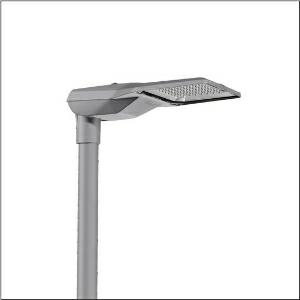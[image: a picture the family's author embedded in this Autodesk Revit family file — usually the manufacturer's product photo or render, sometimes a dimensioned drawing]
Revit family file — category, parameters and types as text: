
# Revit family: streetlight_sl_21_midi___st0_5a_5xe3b33s08lb_3b8c
name_source: partatom
category: Lighting Fixtures
units: mm (PartAtom-declared; Revit-internal decimal feet)

## family parameters
Cut with Voids When Loaded = No
Host = Face
Light Source = No
Part Type = Normal
Room Calculation Point = No
Round Connector Dimension = Use Diameter
Shared = No

## types (1)
- --- (1 x LED, 14340 lm, 99.6 W, 3000K)
    Apparent Load = 100 VA
    CIE Flux Codes = 41 75 97 100 100
    Color Rendering = 70
    Color Temperature = 3000K
    Default Elevation = 1800 mm
    Description = Streetlight SL 21 midi, mast luminaire, primary light control with lens, of PMMA, primary optical cover: cover, of toughened safety glass, transparent, light distribution: ST0.5a, light emission: direct distribution, primary light characteristic: asymmetric, installation type: side-entry, post-top, LED, High Power LED, rated luminous flux: 14.340lm, luminous efficacy: 144lm/W, light colour: 730, colour temperature: 3000K, control gear: D4i, control: overheat protection, constant luminous flux control, time-dependent luminous flux control, flexible luminous flux parameterisation, pre-setting: logarithmic dimming characteristic, mains connection: 230..240V, AC, 50/60Hz, start of lifetime: 100W, end of service life: 102W, reduction: 46W, luminaire housing, of diecast aluminium, powder-coated, Siteco® metallic grey (DB 702S), corrosivity category C5 mid according to DIN EN ISO 12944, please order mast flange separately, inclination adjustable: 0°, 5°, 10°, 15°, sealing non-destructively replaceable, multi-level sealing system, length: 644mm, width: 335mm, height: 110mm, mast flange for spigot size: 42mm (side-entry): 5XC10008XM4, 60/48mm (side-entry/post-top): 5XC10108XM2, 76/60mm (side-entry/post-top): 5XC10108XM1, mounting height: 4..8m, Smart Interface above, protection rating (complete): IP66, insulation class (complete): insulation class II (safety insulation), certification: CE, ENEC, ENEC+, VDE, impact resistance: IK10, permissible operating ambient temperature for outdoor applications: -40..+50°C, standard-compliant lighting for roads and squares, packaging unit: 1 piece

Light Distribution: ST0.5a
    Height = 111 mm
    Lamp = 1 x LED
    Lamp Light Flux = 14340 lm
    Lamp Power = 99.6 W
    Lamp count = 1
    Length = 644 mm
    Luminous efficacy = 144 lm/W
    Manufacturer = Siteco
    ModVariant = No
    Model = 5XE3B33S08LB
    Number of Poles = 1
    OnlyDefault = Yes
    Power Factor = 1
    Product Name = Streetlight SL 21 midi | ST0.5a
    Product group = mast luminaire | pylon top
    ProductGroupID = 6100
    Protection Class = Protection class II
    Protection Degree = IP 66
    RLX_Detail_Level = 1
    RLX_Emergency_Light_Flux = 0 lm
    RLX_Emergency_Type = 0
    RLX_Emergency_Type_DB = No
    RlxData = <blob elided: 37893 chars, md5=fdd6bd25>
    Socket = socket
    Standby Power = 0 W
    System Light Flux = 14340 lm
    System Power = 100 W
    Type Comments = factory setting: luminous flux: 100 % | dim-lin: 254 | 1020 mA
    Type Image = l_1004302.jpg
    URL = http://relux.com
    VarID = @adj_012669
    Voltage = 0 V
    Weight = 0.00 kg
    Width = 336 mm

## geometry (parser evidence)
native form markers: Blend x4, Sweep x13
no freeform markers — native parametric forms only
